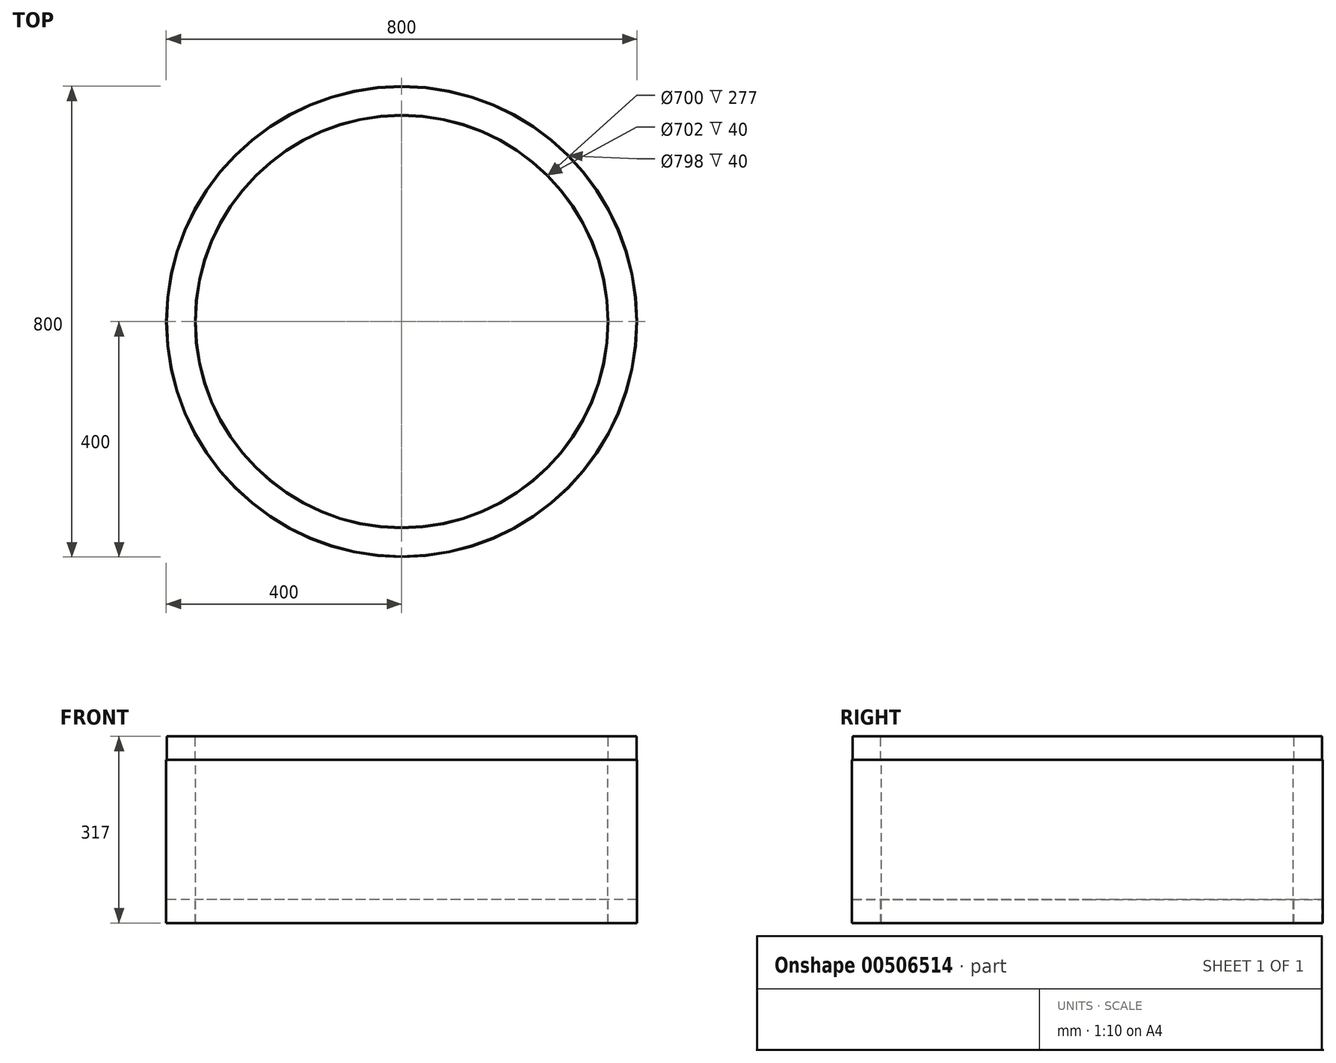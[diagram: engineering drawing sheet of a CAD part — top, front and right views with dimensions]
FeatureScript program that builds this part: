
annotation { "Feature Type Name" : "Feature", "Feature Type Description" : "" }
export const myFeature = defineFeature(function(context is Context, id is Id, definition is map)
    precondition{}
    {
        {
            var Q0;
            Q0=qCreatedBy(makeId("Front.planeOp"),FACE);
            var sketch = newSketch(context, id + "F0", { "sketchPlane" : qUnion([Q0])});
            skLineSegment(sketch, "E0", {"start": v(0, 74.87) * mm, "end": v(0, -73.71) * mm, "construction": true});
            skLineSegment(sketch, "E1", {"start": v(0, 374.84) * mm, "end": v(0, -528.94) * mm, "construction": true});
            skLineSegment(sketch, "E2", {"start": v(-350, -489.75) * mm, "end": v(-350, -212.75) * mm});
            skLineSegment(sketch, "E3", {"start": v(-350, -212.75) * mm, "end": v(-351, -212.75) * mm});
            skLineSegment(sketch, "E4", {"start": v(-351, -212.75) * mm, "end": v(-351, -172.75) * mm});
            skLineSegment(sketch, "E5", {"start": v(-351, -172.75) * mm, "end": v(-399, -172.75) * mm});
            skLineSegment(sketch, "E6", {"start": v(-399, -172.75) * mm, "end": v(-399, -212.75) * mm});
            skLineSegment(sketch, "E7", {"start": v(-399, -212.75) * mm, "end": v(-400, -212.75) * mm});
            skLineSegment(sketch, "E8", {"start": v(-400, -212.75) * mm, "end": v(-400, -489.75) * mm});
            skLineSegment(sketch, "E9", {"start": v(-400, -489.75) * mm, "end": v(-399, -489.75) * mm});
            skLineSegment(sketch, "E10", {"start": v(-399, -489.75) * mm, "end": v(-399, -449.75) * mm});
            skLineSegment(sketch, "E11", {"start": v(-399, -449.75) * mm, "end": v(-351, -449.75) * mm});
            skLineSegment(sketch, "E12", {"start": v(-351, -449.75) * mm, "end": v(-351, -489.75) * mm});
            skLineSegment(sketch, "E13", {"start": v(-351, -489.75) * mm, "end": v(-350, -489.75) * mm});
            skSolve(sketch);
        }
        {
            var Q0;
            Q0=qSketchRegion(id+"F0",true);
            var Q1;
            Q1=sQuery(id+"F0.wireOp",EDGE,"E1");
            revolve(context, id + "F1", {"entities" : qUnion([Q0]), "axis" : qUnion([Q1]), "revolveType" : RevolveType.FULL});
        }
    });
